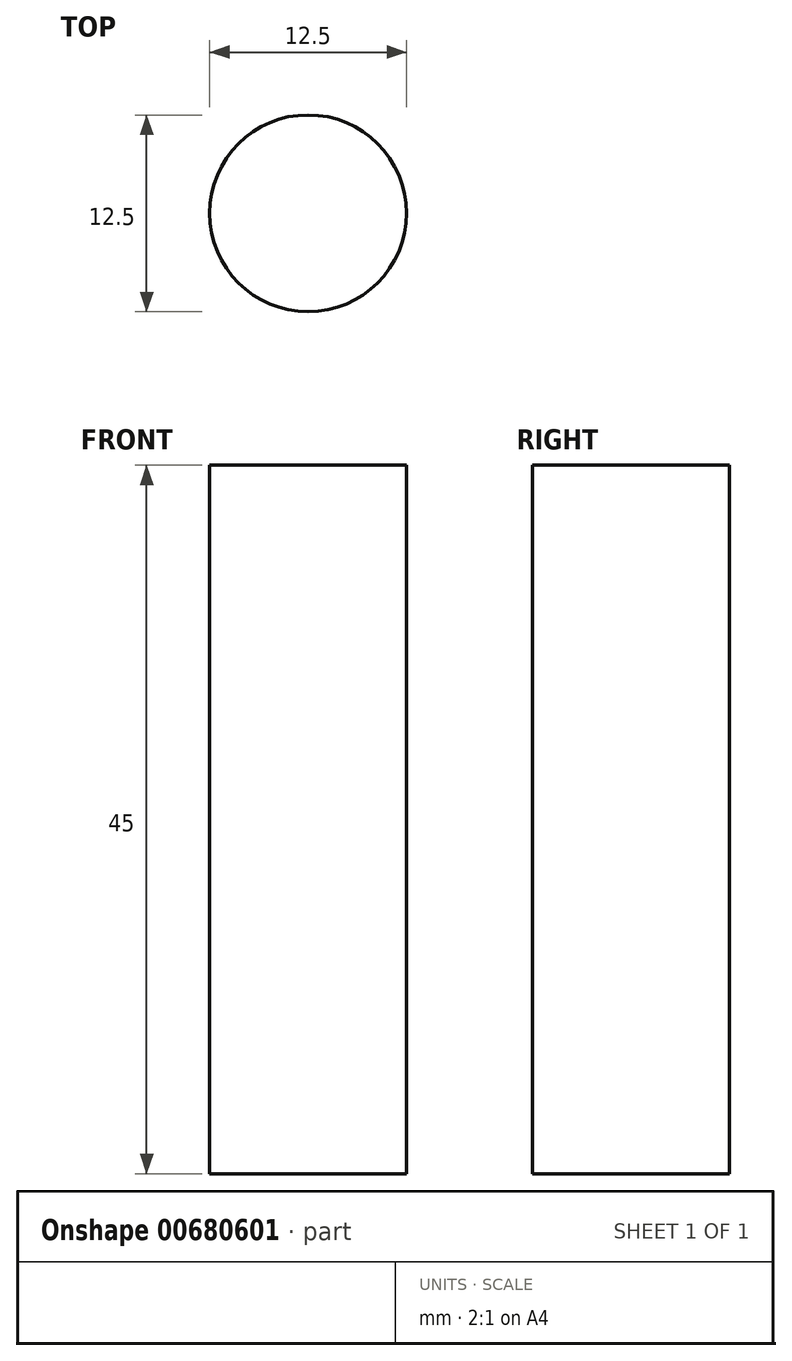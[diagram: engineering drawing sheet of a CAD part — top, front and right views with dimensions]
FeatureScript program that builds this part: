
annotation { "Feature Type Name" : "Feature", "Feature Type Description" : "" }
export const myFeature = defineFeature(function(context is Context, id is Id, definition is map)
    precondition{}
    {
        {
            var Q0;
            Q0=qCreatedBy(makeId("Top.planeOp"),FACE);
            var sketch = newSketch(context, id + "F0", { "sketchPlane" : qUnion([Q0])});
            skCircle(sketch, "E0", {"center": v(0, 0) * mm, "radius": 6.25 * mm});
            skSolve(sketch);
        }
        {
            var Q0;
            Q0=makeQuery(id+"F0.imprint","IMPRINT",FACE,{"disambiguationData":[TD([[makeQuery(id+"F0.imprint","IMPRINT",EDGE,{"derivedFrom":sQuery(id+"F0.wireOp",EDGE,"E0")}),1.0]])]});
            extrude(context, id + "F1", {"entities" : qUnion([Q0]), "depth" : 45 * mm, "offsetDistance" : 25 * mm});
        }
    });
